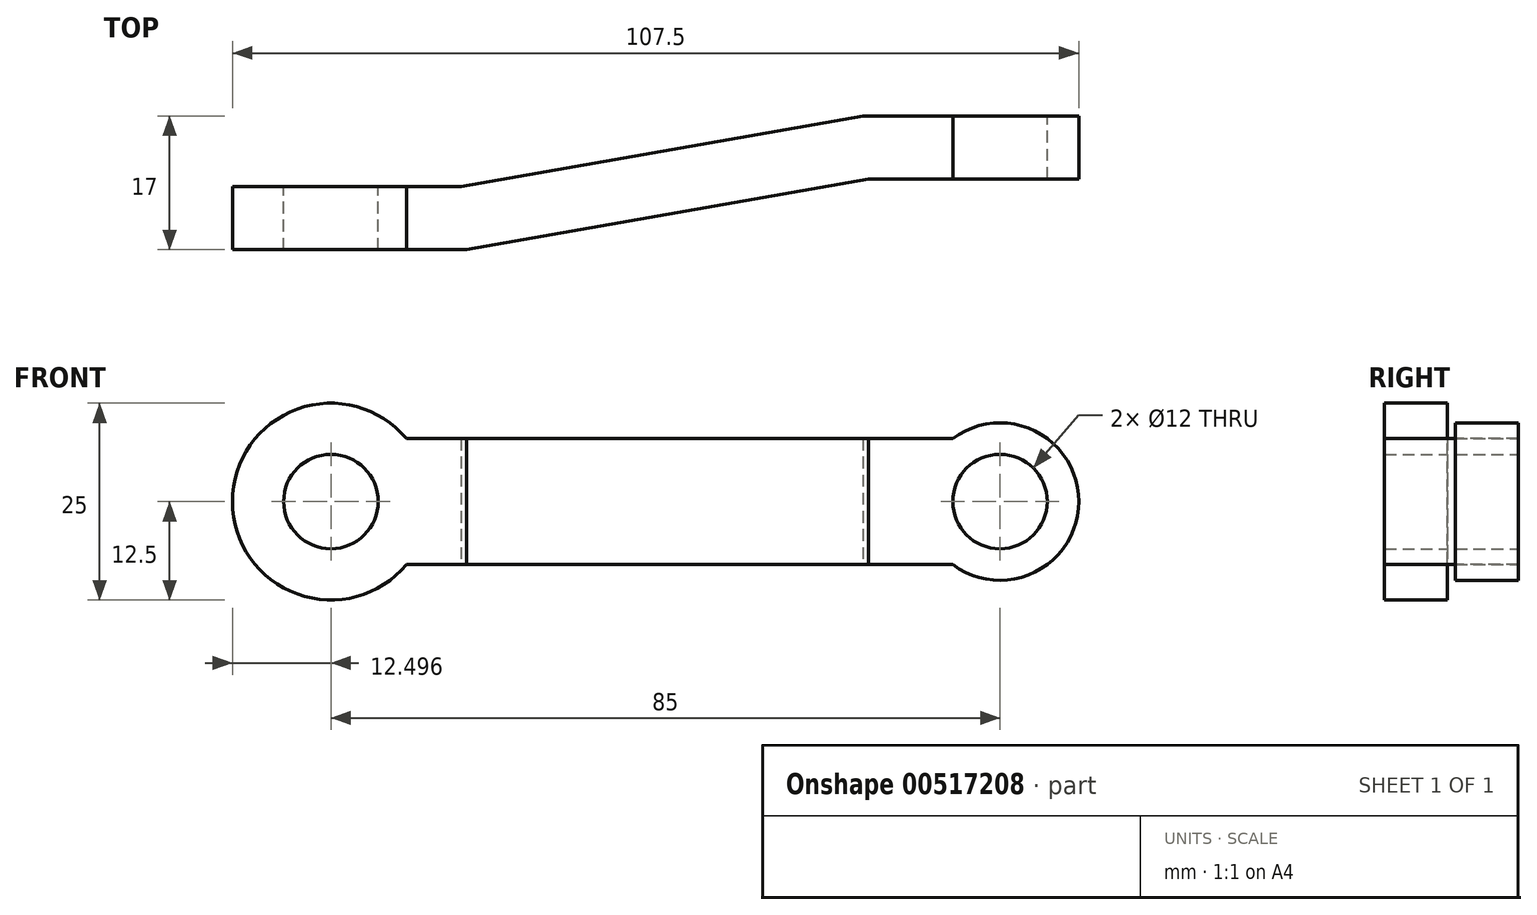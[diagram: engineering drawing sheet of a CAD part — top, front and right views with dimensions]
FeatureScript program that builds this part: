
annotation { "Feature Type Name" : "Feature", "Feature Type Description" : "" }
export const myFeature = defineFeature(function(context is Context, id is Id, definition is map)
    precondition{}
    {
        {
            var Q0;
            Q0=qCreatedBy(makeId("Front.planeOp"),FACE);
            var sketch = newSketch(context, id + "F0", { "sketchPlane" : qUnion([Q0])});
            skCircle(sketch, "E0", {"center": v(-40.31, 0) * mm, "radius": 12.5 * mm});
            skCircle(sketch, "E1", {"center": v(44.69, 0) * mm, "radius": 10 * mm});
            skLineSegment(sketch, "E2", {"start": v(-30.7, 8) * mm, "end": v(38.69, 8) * mm});
            skLineSegment(sketch, "E3.MirrorCS", {"start": v(-30.7, -8) * mm, "end": v(38.69, -8) * mm});
            skCircle(sketch, "E4", {"center": v(-40.31, 0) * mm, "radius": 6 * mm});
            skCircle(sketch, "E5", {"center": v(44.69, 0) * mm, "radius": 6 * mm});
            skSolve(sketch);
        }
        {
            var Q0;
            Q0=makeQuery(id+"F0.imprint","IMPRINT",FACE,{"disambiguationData":[TD([[makeQuery(id+"F0.imprint","IMPRINT",EDGE,{"derivedFrom":sQuery(id+"F0.wireOp",EDGE,"E4")}),-1.0]])]});
            var Q1;
            {var subQ0=sQuery(id+"F0.wireOp",EDGE,"E2");Q1=makeQuery(id+"F0.imprint","IMPRINT",FACE,{"disambiguationData":[TD([[makeQuery(id+"F0.imprint","IMPRINT",EDGE,{"derivedFrom":subQ0}),-1.0]])]});}
            var Q2;
            Q2=makeQuery(id+"F0.imprint","IMPRINT",FACE,{"disambiguationData":[TD([[makeQuery(id+"F0.imprint","IMPRINT",EDGE,{"derivedFrom":sQuery(id+"F0.wireOp",EDGE,"E5")}),-1.0]])]});
            extrude(context, id + "F1", {"entities" : qUnion([Q0, Q1, Q2]), "depth" : 25 * mm, "offsetDistance" : 25 * mm});
        }
        {
            var Q0;
            Q0=qCreatedBy(makeId("Top.planeOp"),FACE);
            var sketch = newSketch(context, id + "F2", { "sketchPlane" : qUnion([Q0])});
            skLineSegment(sketch, "E6", {"start": v(-52.81, -9) * mm, "end": v(-23.78, -9) * mm});
            skLineSegment(sketch, "E7", {"start": v(-23.78, -9) * mm, "end": v(27.26, 0) * mm});
            skLineSegment(sketch, "E8", {"start": v(27.26, 0) * mm, "end": v(54.69, 0) * mm});
            skLineSegment(sketch, "E9.0", {"start": v(27.96, -8) * mm, "end": v(54.69, -8) * mm});
            skLineSegment(sketch, "E9.1", {"start": v(-23.08, -17) * mm, "end": v(27.96, -8) * mm});
            skLineSegment(sketch, "E9.2", {"start": v(-52.81, -17) * mm, "end": v(-23.08, -17) * mm});
            skPoint(sketch, "E10", {"position": v(47.26, 0) * mm});
            skLineSegment(sketch, "E11", {"start": v(10.95, 0) * mm, "end": v(27.26, 0) * mm});
            skLineSegment(sketch, "E12", {"start": v(-52.81, -25) * mm, "end": v(-52.81, 0) * mm});
            skLineSegment(sketch, "E13", {"start": v(54.69, 0) * mm, "end": v(54.69, -25) * mm});
            skSolve(sketch);
        }
        {
            var Q0;
            {var subQ2=sQuery(id+"F2.wireOp",EDGE,"E6");Q0=makeQuery(id+"F2.imprint","IMPRINT",FACE,{"disambiguationData":[TD([[makeQuery(id+"F2.imprint","IMPRINT",EDGE,{"derivedFrom":subQ2}),-1.0]])]});}
            extrude(context, id + "F3", {"entities" : qUnion([Q0]), "operationType" : NewBodyOperationType.INTERSECT, "endBound" : BoundingType.SYMMETRIC, "depth" : 25 * mm, "offsetDistance" : 25 * mm});
        }
    });
